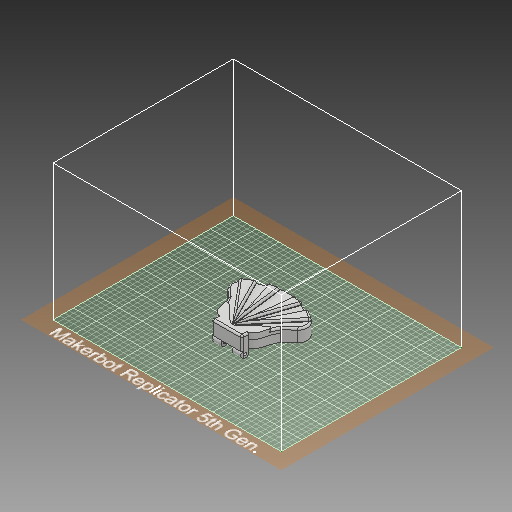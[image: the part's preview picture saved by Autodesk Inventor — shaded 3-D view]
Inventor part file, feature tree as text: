
AUTODESK INVENTOR PART (.ipt)
format: ipt  version: 2018 (Build 220112000, 112)  size: 1,158,144 bytes
history: native  units: in
note: dims shown in document units (in); Inventor stores cm internally (conversion verified against a paired STEP export)
features: sketch x15, plane x12, extrude x11, projected_geometry x4, fillet x3, emboss x1
ambient origin geometry x8: Origin, YZ Plane, XZ Plane, XY Plane, X Axis, Y Axis, Z Axis, Center Point
bodies: Solid1 (feature_tree)
feature tree (46):
  extrude  "Extrusion1"  Depth=1.0in
  plane  "Work Plane1"
  sketch  "Sketch2"  dims[d4=0.1in d5=0.0in d12=0.05in d13=0.0in]
  emboss  "Emboss1"
  extrude  "Extrusion3"  Depth=0.05in TaperAngle=0.0deg
  sketch  "Sketch12"  dims[d21=0.343in d30=0.35in d31=0.0in]
  plane  "Work Plane4"
  plane  "Work Plane9"
  plane  "Work Plane10"
  plane  "Work Plane8"
  extrude  "Extrusion9"  Depth=0.343in
  plane  "Work Plane11"
  plane  "Work Plane12"
  plane  "Work Plane13"
  sketch  "Sketch22"  dims[d60=1214.0in d61=0.0in d62=0.3in d63=0.0in]
  plane  "Work Plane16"
  extrude  "Extrusion14"  Depth=0.35in TaperAngle=0.0deg
  plane  "Work Plane17"
  extrude  "Extrusion15"  Depth=0.42in
  plane  "Work Plane14"
  extrude  "Extrusion16"  Depth=0.126in
  extrude  "Extrusion17"  Depth=0.3in TaperAngle=0.0deg
  extrude  "Extrusion18"  Depth=0.3in TaperAngle=0.0deg
  fillet  "Fillet10"  Radius=0.0787in
  fillet  "Fillet12"  Radius=0.0787in
  fillet  "Fillet14"  Radius=0.0787in
  plane  "Work Plane18"
  extrude  "Extrusion19"  Depth=9.1339in TaperAngle=0.0deg
  extrude  "Extrusion20"  Depth=0.2112in
  extrude  "Extrusion21"  Depth=0.0984in
  sketch  "Sketch17"  dims[d55=0.42in d56=0.42in]
  sketch  "Sketch1"  dims[d0=0.3in d1=0.0in d2=1.0in]
  sketch  "Sketch9"  dims[d19=3.017in d20=0.343in]
  projected_geometry  "Projected Loop2"
  projected_geometry  "Projected Loop3"
  sketch  "Sketch18"  dims[d57=1.0in d58=0.0in d59=0.126in]
  sketch  "Sketch24"  dims[d64=10.0in d65=0.0in d66=0.3in d67=0.0in d68=0.0787in d70=0.0787in d72=0.0787in]
  sketch  "Sketch25"  dims[d73=0.6102in d74=9.1339in d75=0.0in]
  sketch  "Sketch26"  dims[d76=3.0709in d77=0.0in d78=0.2112in]
  sketch  "Sketch27"  dims[d79=0.2854in d80=0.0984in]
  sketch  "Sketch28"  dims[d81=0.3937in d82=0.0in]
  sketch  "Sketch30"  dims[d83=0.1969in]
  projected_geometry  "Projected Loop5"
  sketch  "Sketch31"
  sketch  "Sketch32"
  projected_geometry  "Projected Loop7"
